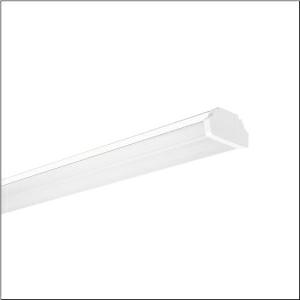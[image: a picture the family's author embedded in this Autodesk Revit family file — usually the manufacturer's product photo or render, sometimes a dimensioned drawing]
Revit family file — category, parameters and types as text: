
# Revit family: modario_31_gen_2_53bm813mv4a5c2_5524
name_source: partatom
category: Lighting Fixtures
units: mm (PartAtom-declared; Revit-internal decimal feet)

## family parameters
Cut with Voids When Loaded = No
Host = Face
Light Source = No
Part Type = Normal
Room Calculation Point = No
Round Connector Dimension = Use Diameter
Shared = No

## types (1)
- --- (1 x LED, 10710 lm, 60.5 W, 4000K)
    Apparent Load = 61 VA
    CIE Flux Codes = 62 83 95 93 100
    Color Rendering = 80
    Color Temperature = 4000K
    Default Elevation = 1800 mm
    Description = Modario 31 Gen.2, luminaire insert, of sheet steel, coil coated, white, length: 1.495mm, width: 81mm, height: 82mm, 5x system unit, system units: 299mm, LED rated luminous flux: 10.710lm, light colour: 840, SDCM (Standard Deviation of Colour Matching)MacAdam ≤ 3 SDCM (initial), control gear: ON/OFF Multilumen, control gear: ECG, with plug, 3-pole, with phase selection, mains connection: 220..240V, AC, 50/60Hz, rated input power: 61W, through-wiring accessed according to module size, primary optical cover: cover, of PMMA, light emission: direct distribution, primary light characteristic: symmetric, protection rating (complete): IP20, protection rating (LED compartment): IP50, insulation class (complete): insulation class I (protective earthing), certification: CE, ENEC, VDE, UKCA, impact resistance: IK03, permissible ambient temperature for indoor applications: -35..+40°C, corresponds to IFS (International Featured Standards) requirements for safety and quality in the food industry, reducing of maximum allowable ambient temperature of 5°C with ceiling mounting, IP40 when using the optional accessory 5TP9018, packaging unit: 1 piece
    Height = 92 mm
    Lamp = 1 x LED
    Lamp Light Flux = 10710 lm
    Lamp Power = 60.5 W
    Lamp count = 1
    Length = 1495 mm
    Luminous efficacy = 177 lm/W
    Manufacturer = Siteco
    ModVariant = No
    Model = 53BM813MV4A5C2
    Mounting Place = Ceiling
    Mounting Type = Pendant
    Number of Poles = 1
    OnlyDefault = Yes
    Power Factor = 1
    Product Name = Modario 31 Gen.2
    Product group = luminaire insert | ceiling pendant
    ProductGroupID = 901
    Protection Class = Protection class I
    Protection Degree = IP 20
    RLX_Detail_Level = 1
    RLX_Emergency_Light_Flux = 0 lm
    RLX_Emergency_Type = 0
    RLX_Emergency_Type_DB = No
    RlxData = <blob elided: 39989 chars, md5=f2787824>
    Socket = socket
    Standby Power = 0 W
    System Light Flux = 10710 lm
    System Power = 61 W
    Type Comments = factory setting: luminous flux: 100 % | (A | C | E) | 140 mA
    Type Image = l_1341886.jpg
    URL = http://relux.com
    VarID = @adj_002241
    Voltage = 0 V
    Weight = 0.00 kg
    Width = 81 mm

## geometry (parser evidence)
native form markers: Blend x4, Sweep x11
no freeform markers — native parametric forms only
